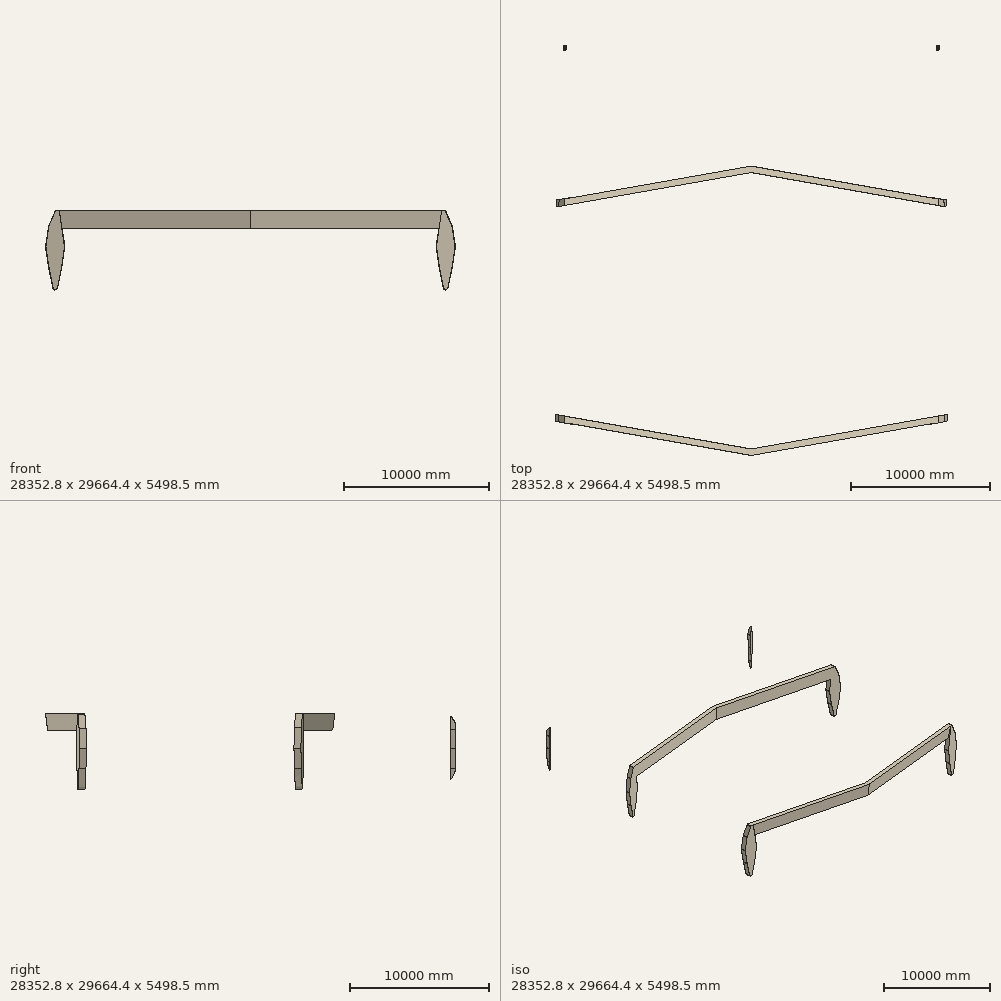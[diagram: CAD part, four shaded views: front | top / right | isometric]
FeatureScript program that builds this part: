
annotation { "Feature Type Name" : "Feature", "Feature Type Description" : "" }
export const myFeature = defineFeature(function(context is Context, id is Id, definition is map)
    precondition{}
    {
        {
            var Q0;
            Q0=qCreatedBy(makeId("Front.planeOp"),FACE);
            var sketch = newSketch(context, id + "F0", { "sketchPlane" : qUnion([Q0])});
            skPoint(sketch, "E0.end.orphan", {"position": v(0, 0) * mm});
            skLineSegment(sketch, "E1", {"start": v(0, 0) * mm, "end": v(0, -5500) * mm});
            skLineSegment(sketch, "E2", {"start": v(500, -4000) * mm, "end": v(750, -2500) * mm});
            skFitSpline(sketch, "E3", {"points": [v(0, -5500) * mm, v(189.72, -5319.94) * mm, v(366.95, -4555.93) * mm, v(500, -4000) * mm], "startDerivative": vector(1833.22, 785.24) * mm, "endDerivative": vector(535.36, 2334.8) * mm});
            skLineSegment(sketch, "E4", {"start": v(0, 0) * mm, "end": v(500, -1000) * mm});
            skLineSegment(sketch, "E5", {"start": v(500, -1000) * mm, "end": v(750, -2500) * mm});
            skSolve(sketch);
        }
        {
            var Q0;
            Q0=qCreatedBy(makeId("Front.planeOp"),FACE);
            cPlane(context, id + "F1", {"entities" : qUnion([Q0]), "cplaneType" : CPlaneType.OFFSET, "offset" : 10000 * mm, "oppositeDirection" : true, "width" : 150 * mm, "height" : 150 * mm});
        }
        {
            var Q0;
            Q0=qCreatedBy(id+"F1.planeOp",FACE);
            var sketch = newSketch(context, id + "F2", { "sketchPlane" : qUnion([Q0])});
            skLineSegment(sketch, "E6", {"start": v(0, 0) * mm, "end": v(0, -5500) * mm});
            skFitSpline(sketch, "E7", {"points": [v(0, -5500) * mm, v(174.15, -5265.2) * mm, v(305.11, -4690.98) * mm, v(500, -4000) * mm], "startDerivative": vector(1750.56, 1279.5) * mm, "endDerivative": vector(993.95, 3484.4) * mm});
            skLineSegment(sketch, "E8", {"start": v(500, -4000) * mm, "end": v(750, -2500) * mm});
            skPoint(sketch, "E9.startDerivative.orphan", {"position": v(5091.83, 0) * mm});
            skLineSegment(sketch, "E10", {"start": v(500, -1000) * mm, "end": v(0, 0) * mm});
            skLineSegment(sketch, "E11", {"start": v(750, -2500) * mm, "end": v(500, -1000) * mm});
            skSolve(sketch);
        }
        {
            var Q0;
            Q0=qCreatedBy(id+"F1.planeOp",FACE);
            cPlane(context, id + "F3", {"entities" : qUnion([Q0]), "cplaneType" : CPlaneType.OFFSET, "offset" : 15000 * mm, "oppositeDirection" : true, "width" : 150 * mm, "height" : 150 * mm});
        }
        {
            var Q0;
            Q0=qCreatedBy(id+"F3.planeOp",FACE);
            var sketch = newSketch(context, id + "F4", { "sketchPlane" : qUnion([Q0])});
            skLineSegment(sketch, "E12", {"start": v(0, 0) * mm, "end": v(0, -5500) * mm});
            skLineSegment(sketch, "E13", {"start": v(0, -5500) * mm, "end": v(0, -5500) * mm});
            skLineSegment(sketch, "E14", {"start": v(0, -5500) * mm, "end": v(12.9, -4000) * mm});
            skLineSegment(sketch, "E15", {"start": v(12.9, -4000) * mm, "end": v(85.66, -2500) * mm});
            skLineSegment(sketch, "E16", {"start": v(0, 0) * mm, "end": v(94.2, -1134.32) * mm});
            skLineSegment(sketch, "E17", {"start": v(94.2, -1134.32) * mm, "end": v(85.66, -2500) * mm});
            skSolve(sketch);
        }
        {
            var Q0;
            Q0=qCreatedBy(makeId("Front.planeOp"),FACE);
            cPlane(context, id + "F5", {"entities" : qUnion([Q0]), "cplaneType" : CPlaneType.OFFSET, "offset" : 10000 * mm, "width" : 150 * mm, "height" : 150 * mm});
        }
        {
            var Q0;
            Q0=qCreatedBy(id+"F5.planeOp",FACE);
            var sketch = newSketch(context, id + "F6", { "sketchPlane" : qUnion([Q0])});
            skLineSegment(sketch, "E18", {"start": v(0, -500) * mm, "end": v(0, -5500) * mm});
            skLineSegment(sketch, "E19", {"start": v(0, -5500) * mm, "end": v(14.37, -4000) * mm});
            skLineSegment(sketch, "E20", {"start": v(14.37, -4000) * mm, "end": v(85.96, -2500) * mm});
            skPoint(sketch, "E21", {"position": v(51.72, -1902.5) * mm});
            skLineSegment(sketch, "E22", {"start": v(94.34, -1565.05) * mm, "end": v(85.96, -2500) * mm});
            skLineSegment(sketch, "E23", {"start": v(0, -500) * mm, "end": v(94.34, -1565.05) * mm});
            skSolve(sketch);
        }
        {
            var Q0;
            Q0=makeQuery(id+"F4.imprint","IMPRINT",FACE,{"disambiguationData":[TD([[makeQuery(id+"F4.imprint","IMPRINT",EDGE,{"derivedFrom":sQuery(id+"F4.wireOp",EDGE,"E12")}),1.0]])]});
            var Q1;
            Q1=makeQuery(id+"F2.imprint","IMPRINT",FACE,{"disambiguationData":[TD([[makeQuery(id+"F2.imprint","IMPRINT",EDGE,{"derivedFrom":sQuery(id+"F2.wireOp",EDGE,"E6")}),1.0]])]});
            var Q2;
            Q2=makeQuery(id+"F0.imprint","IMPRINT",FACE,{"disambiguationData":[TD([[makeQuery(id+"F0.imprint","IMPRINT",EDGE,{"derivedFrom":sQuery(id+"F0.wireOp",EDGE,"E1")}),1.0]])]});
            var Q3;
            Q3=makeQuery(id+"F6.imprint","IMPRINT",FACE,{"disambiguationData":[TD([[makeQuery(id+"F6.imprint","IMPRINT",EDGE,{"derivedFrom":sQuery(id+"F6.wireOp",EDGE,"E18")}),1.0]])]});
            var Q4;
            Q4=sQuery(id+"F4.wireOp",EDGE,"E14");
            var Q5;
            Q5=sQuery(id+"F2.wireOp",EDGE,"E8");
            var Q6;
            Q6=sQuery(id+"F4.wireOp",EDGE,"E15");
            var Q7;
            Q7=sQuery(id+"F4.wireOp",EDGE,"sgJCfSwm-QjFF-VmRN-4AcW-iuittDDyERBM");
            loft(context, id + "F7", {"sheetProfilesArray" : [{ "sheetProfileEntities" : qUnion([Q0]) }, { "sheetProfileEntities" : qUnion([Q1]) }, { "sheetProfileEntities" : qUnion([Q2]) }, { "sheetProfileEntities" : qUnion([Q3]) }], "guidesArray" : [{ "guideEntities" : qUnion([Q4]), "guideDerivativeType" : LoftGuideDerivativeType.DEFAULT, "guideDerivativeMagnitude" : 1 }, { "guideEntities" : qUnion([Q5]), "guideDerivativeType" : LoftGuideDerivativeType.DEFAULT, "guideDerivativeMagnitude" : 1 }, { "guideEntities" : qUnion([Q6]), "guideDerivativeType" : LoftGuideDerivativeType.DEFAULT, "guideDerivativeMagnitude" : 1 }, { "guideEntities" : qUnion([Q7]), "guideDerivativeType" : LoftGuideDerivativeType.DEFAULT, "guideDerivativeMagnitude" : 1 }]});
        }
        {
            var Q0;
            Q0=makeQuery(id+"F7.opLoft","SWEPT_BODY",BODY,{"disambiguationData":[OSD([sQuery(id+"F0.wireOp",EDGE,"E3"),sQuery(id+"F2.wireOp",EDGE,"E7"),makeQuery(id+"F4.imprint","IMPRINT",FACE,{"disambiguationData":[TD([[makeQuery(id+"F4.imprint","IMPRINT",EDGE,{"derivedFrom":sQuery(id+"F4.wireOp",EDGE,"E12")}),1.0]])]}),makeQuery(id+"F6.imprint","IMPRINT",FACE,{"disambiguationData":[TD([[makeQuery(id+"F6.imprint","IMPRINT",EDGE,{"derivedFrom":sQuery(id+"F6.wireOp",EDGE,"E18")}),1.0]])]})])]});
            var Q1;
            Q1=qCreatedBy(makeId("Right.planeOp"),FACE);
            mirror(context, id + "F8", {"operationType" : NewBodyOperationType.ADD, "entities" : qUnion([Q0]), "mirrorPlane" : qUnion([Q1])});
        }
        {
            var Q0;
            {var subQ0=makeQuery(id+"F7.opLoft","SWEPT_EDGE",EDGE,{"disambiguationData":[OSD([sQuery(id+"F0.wireOp",EDGE,"E1"),sQuery(id+"F0.wireOp",EDGE,"E3"),sQuery(id+"F6.wireOp",EDGE,"E18"),sQuery(id+"F6.wireOp",EDGE,"E19")])]});Q0=makeQuery(id+"F8.boolean.opBoolean","MERGE",EDGE,{"derivedFrom":[subQ0,makeQuery(id+"F8.opPattern","COPY",EDGE,{"derivedFrom":subQ0,"instanceName":"1"})]});}
            fillet(context, id + "F9", {"entities" : qUnion([Q0]), "radius" : 12 * mm, "tangentPropagation" : true, "allowEdgeOverflow" : false});
        }
        {
            var Q0;
            Q0=qCreatedBy(makeId("Front.planeOp"),FACE);
            var sketch = newSketch(context, id + "F10", { "sketchPlane" : qUnion([Q0])});
            skLineSegment(sketch, "E24", {"start": v(0, 0) * mm, "end": v(0, -5082.07) * mm, "construction": true});
            skLineSegment(sketch, "E25", {"start": v(-7000, 3102.27) * mm, "end": v(-7000, -5771.46) * mm, "construction": true});
            skLineSegment(sketch, "E26", {"start": v(-7000, 0) * mm, "end": v(-13500, 0) * mm});
            skLineSegment(sketch, "E27", {"start": v(-13500, 0) * mm, "end": v(-13500, -1000) * mm});
            skLineSegment(sketch, "E28", {"start": v(-13500, -1000) * mm, "end": v(-7000, -1000) * mm});
            skLineSegment(sketch, "E29", {"start": v(-7000, -1000) * mm, "end": v(0, -1000) * mm});
            skLineSegment(sketch, "E30", {"start": v(0, 0) * mm, "end": v(0, -1000) * mm});
            skLineSegment(sketch, "E31", {"start": v(-7000, 0) * mm, "end": v(0, 0) * mm});
            skSolve(sketch);
        }
        {
            var Q0;
            Q0=makeQuery(id+"F10.imprint","IMPRINT",FACE,{"disambiguationData":[TD([[makeQuery(id+"F10.imprint","IMPRINT",EDGE,{"derivedFrom":sQuery(id+"F10.wireOp",EDGE,"3sFQAXWc-wyO7-hPk9-7dSX-oAIZwABY1ojd")}),1.0]])]});
            var Q1;
            Q1=makeQuery(id+"F10.imprint","IMPRINT",FACE,{"disambiguationData":[TD([[makeQuery(id+"F10.imprint","IMPRINT",EDGE,{"derivedFrom":sQuery(id+"F10.wireOp",EDGE,"E26")}),1.0]])]});
            extrude(context, id + "F11", {"entities" : qUnion([Q0, Q1]), "endBound" : BoundingType.SYMMETRIC, "oppositeDirection" : true, "depth" : 37400 * mm});
        }
        {
            var Q0;
            Q0=qCreatedBy(makeId("Top.planeOp"),FACE);
            var sketch = newSketch(context, id + "F12", { "sketchPlane" : qUnion([Q0])});
            skLineSegment(sketch, "E32.bottom", {"start": v(-13500, 24621.28) * mm, "end": v(7276.55, 24621.28) * mm});
            skLineSegment(sketch, "E32.left", {"start": v(-13500, 24621.28) * mm, "end": v(-13500, 16304.47) * mm});
            skLineSegment(sketch, "E32.right", {"start": v(7276.55, 24621.28) * mm, "end": v(7276.55, 18829) * mm});
            skLineSegment(sketch, "E33.left", {"start": v(-13500, 15804.47) * mm, "end": v(-13500, -4195.53) * mm});
            skLineSegment(sketch, "E33.right", {"start": v(8153.2, 18329) * mm, "end": v(8153.2, -1671) * mm});
            skLineSegment(sketch, "E34.top", {"start": v(-13500, -21040.08) * mm, "end": v(8250.14, -21040.08) * mm});
            skLineSegment(sketch, "E34.left", {"start": v(-13500, -4695.53) * mm, "end": v(-13500, -21040.08) * mm});
            skLineSegment(sketch, "E34.right", {"start": v(8250.14, -2171) * mm, "end": v(8250.14, -21040.08) * mm});
            skLineSegment(sketch, "E35", {"start": v(0, -1047.14) * mm, "end": v(-1927.45, -1047.14) * mm, "construction": true});
            skLineSegment(sketch, "E36", {"start": v(0, 2086.97) * mm, "end": v(-2089.7, 2086.97) * mm, "construction": true});
            skLineSegment(sketch, "E37", {"start": v(-13500, 23613.23) * mm, "end": v(-13500, -27703.45) * mm, "construction": true});
            skLineSegment(sketch, "E38", {"start": v(-13500, 16304.47) * mm, "end": v(8153.2, 12486.43) * mm});
            skLineSegment(sketch, "E39", {"start": v(-13500, 15804.47) * mm, "end": v(8153.2, 11986.43) * mm});
            skLineSegment(sketch, "E40", {"start": v(-13500, -4195.53) * mm, "end": v(8153.2, -377.49) * mm});
            skLineSegment(sketch, "E41", {"start": v(-13500, -4695.53) * mm, "end": v(8153.2, -877.49) * mm});
            skLineSegment(sketch, "E42", {"start": v(7276.55, 18829) * mm, "end": v(8153.2, 18329) * mm});
            skLineSegment(sketch, "E43", {"start": v(8153.2, -1671) * mm, "end": v(8250.14, -2171) * mm});
            skSolve(sketch);
        }
        {
            var Q0;
            Q0=makeQuery(id+"F12.imprint","IMPRINT",FACE,{"disambiguationData":[TD([[makeQuery(id+"F12.imprint","IMPRINT",EDGE,{"derivedFrom":sQuery(id+"F12.wireOp",EDGE,"E32.bottom")}),-1.0]])]});
            var Q1;
            Q1=makeQuery(id+"F12.imprint","IMPRINT",FACE,{"disambiguationData":[TD([[makeQuery(id+"F12.imprint","IMPRINT",EDGE,{"derivedFrom":sQuery(id+"F12.wireOp",EDGE,"E33.left")}),1.0]])]});
            var Q2;
            Q2=makeQuery(id+"F12.imprint","IMPRINT",FACE,{"disambiguationData":[TD([[makeQuery(id+"F12.imprint","IMPRINT",EDGE,{"derivedFrom":sQuery(id+"F12.wireOp",EDGE,"E34.top")}),1.0]])]});
            extrude(context, id + "F13", {"entities" : qUnion([Q0, Q1, Q2]), "operationType" : NewBodyOperationType.REMOVE, "endBound" : BoundingType.SYMMETRIC, "oppositeDirection" : true, "depth" : 13225 * mm});
        }
        {
            var Q0;
            Q0=makeQuery(id+"F7.opLoft","SWEPT_BODY",BODY,{"disambiguationData":[OSD([sQuery(id+"F0.wireOp",EDGE,"E4"),sQuery(id+"F2.wireOp",EDGE,"E8"),makeQuery(id+"F4.imprint","IMPRINT",FACE,{"disambiguationData":[TD([[makeQuery(id+"F4.imprint","IMPRINT",EDGE,{"derivedFrom":sQuery(id+"F4.wireOp",EDGE,"E12")}),1.0]])]}),makeQuery(id+"F6.imprint","IMPRINT",FACE,{"disambiguationData":[TD([[makeQuery(id+"F6.imprint","IMPRINT",EDGE,{"derivedFrom":sQuery(id+"F6.wireOp",EDGE,"E18")}),1.0]])]})])]});
            var Q1;
            Q1=makeQuery(id+"F11.opExtrude","SWEPT_BODY",BODY,{"disambiguationData":[OSD([sQuery(id+"F10.wireOp",EDGE,"E26"),sQuery(id+"F10.wireOp",EDGE,"E27"),sQuery(id+"F10.wireOp",EDGE,"E28"),sQuery(id+"F10.wireOp",EDGE,"E29"),sQuery(id+"F10.wireOp",EDGE,"E30"),sQuery(id+"F10.wireOp",EDGE,"E31")])]});
            var Q2;
            Q2=makeQuery(id+"F11.opExtrude","SWEPT_FACE",FACE,{"disambiguationData":[OSD([sQuery(id+"F10.wireOp",EDGE,"E27")])]});
            mirror(context, id + "F14", {"operationType" : NewBodyOperationType.ADD, "entities" : qUnion([Q0, Q1]), "mirrorPlane" : qUnion([Q2])});
        }
        {
            var Q0;
            Q0=qCreatedBy(makeId("Right.planeOp"),FACE);
            var sketch = newSketch(context, id + "F15", { "sketchPlane" : qUnion([Q0])});
            skLineSegment(sketch, "E44", {"start": v(25015.3, -3553.39) * mm, "end": v(25015.3, -1000) * mm});
            skLineSegment(sketch, "E45", {"start": v(24015.3, 0) * mm, "end": v(13594.14, 0) * mm});
            skLineSegment(sketch, "E46", {"start": v(13594.14, 0) * mm, "end": v(12052.37, 3741.26) * mm});
            skLineSegment(sketch, "E47", {"start": v(12052.37, 3741.26) * mm, "end": v(25847.84, 3035.2) * mm});
            skLineSegment(sketch, "E48", {"start": v(25847.84, 3035.2) * mm, "end": v(26929.87, 1249.84) * mm});
            skLineSegment(sketch, "E49", {"start": v(26929.87, 1249.84) * mm, "end": v(25015.3, -3553.39) * mm});
            skPoint(sketch, "E50.visualSharp", {"position": v(25015.3, 0) * mm});
            skArc(sketch, "E50.filletArc", {"start": v(25015.3, -1000) * mm, "mid": v(24722.4, -292.9) * mm, "end": v(24015.3, 0) * mm});
            skLineSegment(sketch, "E51", {"start": v(-10015.9, -1415.8) * mm, "end": v(-10015.9, -3965.22) * mm});
            skLineSegment(sketch, "E52", {"start": v(-10015.9, -3965.22) * mm, "end": v(-12936.5, -3419.61) * mm});
            skLineSegment(sketch, "E53", {"start": v(-12936.5, -3419.61) * mm, "end": v(-12936.5, 1047.72) * mm});
            skLineSegment(sketch, "E54", {"start": v(-12936.5, 1047.72) * mm, "end": v(-5974.96, 1396.63) * mm});
            skPoint(sketch, "E55.visualSharp", {"position": v(-10015.9, 0) * mm});
            skPoint(sketch, "E56.visualSharp", {"position": v(-10015.9, -509.7) * mm});
            skArc(sketch, "E56.filletArc", {"start": v(-9114.2, -420.64) * mm, "mid": v(-9756.95, -744.34) * mm, "end": v(-10015.9, -1415.8) * mm});
            skLineSegment(sketch, "E57", {"start": v(-5974.96, 1396.63) * mm, "end": v(-4930.65, -171.54) * mm});
            skLineSegment(sketch, "E58", {"start": v(-4930.65, -171.54) * mm, "end": v(-9114.2, -420.64) * mm});
            skSolve(sketch);
        }
        {
            var Q0;
            Q0=makeQuery(id+"F15.imprint","IMPRINT",FACE,{"disambiguationData":[TD([[makeQuery(id+"F15.imprint","IMPRINT",EDGE,{"derivedFrom":sQuery(id+"F15.wireOp",EDGE,"E51")}),-1.0]])]});
            var Q1;
            Q1=makeQuery(id+"F15.imprint","IMPRINT",FACE,{"disambiguationData":[TD([[makeQuery(id+"F15.imprint","IMPRINT",EDGE,{"derivedFrom":sQuery(id+"F15.wireOp",EDGE,"E44")}),-1.0]])]});
            extrude(context, id + "F16", {"entities" : qUnion([Q0, Q1]), "operationType" : NewBodyOperationType.REMOVE, "endBound" : BoundingType.SYMMETRIC, "oppositeDirection" : true, "depth" : 88000 * mm});
        }
        {
            var Q0;
            {var subQ0=makeQuery(id+"F13.boolean.opBoolean","SPLIT",FACE,{"disambiguationData":[TD([makeQuery(id+"F13.opExtrude","SWEPT_FACE",FACE,{"disambiguationData":[OSD([sQuery(id+"F12.wireOp",EDGE,"E40")])]})])],"derivedFrom":makeQuery(id+"F11.opExtrude","SWEPT_FACE",FACE,{"disambiguationData":[OSD([sQuery(id+"F10.wireOp",EDGE,"E28"),sQuery(id+"F10.wireOp",EDGE,"E29")])]})});Q0=makeQuery(id+"F14.boolean.opBoolean","MERGE",FACE,{"derivedFrom":[subQ0,makeQuery(id+"F14.opPattern","COPY",FACE,{"derivedFrom":subQ0,"instanceName":"1"})]});}
            var Q1;
            {var subQ0=makeQuery(id+"F13.boolean.opBoolean","SPLIT",FACE,{"disambiguationData":[TD([makeQuery(id+"F13.opExtrude","SWEPT_FACE",FACE,{"disambiguationData":[OSD([sQuery(id+"F12.wireOp",EDGE,"E38")])]})])],"derivedFrom":makeQuery(id+"F11.opExtrude","SWEPT_FACE",FACE,{"disambiguationData":[OSD([sQuery(id+"F10.wireOp",EDGE,"E28"),sQuery(id+"F10.wireOp",EDGE,"E29")])]})});Q1=makeQuery(id+"F14.boolean.opBoolean","MERGE",FACE,{"derivedFrom":[subQ0,makeQuery(id+"F14.opPattern","COPY",FACE,{"derivedFrom":subQ0,"instanceName":"1"})]});}
            extrude(context, id + "F17", {"entities" : qUnion([Q0, Q1]), "operationType" : NewBodyOperationType.ADD, "depth" : 250 * mm});
        }
        {
            var Q0;
            {var subQ0=sQuery(id+"F12.wireOp",EDGE,"E41");var subQ1=sQuery(id+"F10.wireOp",EDGE,"E29");var subQ2=sQuery(id+"F10.wireOp",EDGE,"E28");Q0=makeQuery(id+"F17.opExtrude","CAP_EDGE",EDGE,{"disambiguationData":[OSD([subQ2,subQ1,subQ0]),TDD([makeQuery(id+"F13.boolean.opBoolean","INTERSECT",EDGE,{"derivedFrom":[makeQuery(id+"F11.opExtrude","SWEPT_FACE",FACE,{"disambiguationData":[OSD([subQ2,subQ1])]}),makeQuery(id+"F13.opExtrude","SWEPT_FACE",FACE,{"disambiguationData":[OSD([subQ0])]})]})])],"isStart":false});}
            var Q1;
            {var subQ0=sQuery(id+"F12.wireOp",EDGE,"E41");var subQ1=sQuery(id+"F10.wireOp",EDGE,"E29");var subQ2=sQuery(id+"F10.wireOp",EDGE,"E28");Q1=makeQuery(id+"F17.opExtrude","CAP_EDGE",EDGE,{"disambiguationData":[OSD([subQ2,subQ1,subQ0]),TDD([makeQuery(id+"F14.opPattern","COPY",EDGE,{"derivedFrom":makeQuery(id+"F13.boolean.opBoolean","INTERSECT",EDGE,{"derivedFrom":[makeQuery(id+"F11.opExtrude","SWEPT_FACE",FACE,{"disambiguationData":[OSD([subQ2,subQ1])]}),makeQuery(id+"F13.opExtrude","SWEPT_FACE",FACE,{"disambiguationData":[OSD([subQ0])]})]}),"instanceName":"1"})])],"isStart":false});}
            var Q2;
            {var subQ0=sQuery(id+"F12.wireOp",EDGE,"E38");var subQ1=sQuery(id+"F10.wireOp",EDGE,"E29");var subQ2=sQuery(id+"F10.wireOp",EDGE,"E28");Q2=makeQuery(id+"F17.opExtrude","CAP_EDGE",EDGE,{"disambiguationData":[OSD([subQ2,subQ1,subQ0]),TDD([makeQuery(id+"F14.opPattern","COPY",EDGE,{"derivedFrom":makeQuery(id+"F13.boolean.opBoolean","INTERSECT",EDGE,{"derivedFrom":[makeQuery(id+"F11.opExtrude","SWEPT_FACE",FACE,{"disambiguationData":[OSD([subQ2,subQ1])]}),makeQuery(id+"F13.opExtrude","SWEPT_FACE",FACE,{"disambiguationData":[OSD([subQ0])]})]}),"instanceName":"1"})])],"isStart":false});}
            chamfer(context, id + "F18", {"entities" : qUnion([Q0, Q1, Q2]), "chamferType" : ChamferType.OFFSET_ANGLE, "width" : 1500 * mm, "oppositeDirection" : true, "angle" : 7 * degree, "tangentPropagation" : true});
        }
        {
            var Q0;
            {var subQ0=sQuery(id+"F12.wireOp",EDGE,"E38");var subQ1=sQuery(id+"F10.wireOp",EDGE,"E29");var subQ2=sQuery(id+"F10.wireOp",EDGE,"E28");Q0=makeQuery(id+"F17.opExtrude","CAP_EDGE",EDGE,{"disambiguationData":[OSD([subQ2,subQ1,subQ0]),TDD([makeQuery(id+"F13.boolean.opBoolean","INTERSECT",EDGE,{"derivedFrom":[makeQuery(id+"F11.opExtrude","SWEPT_FACE",FACE,{"disambiguationData":[OSD([subQ2,subQ1])]}),makeQuery(id+"F13.opExtrude","SWEPT_FACE",FACE,{"disambiguationData":[OSD([subQ0])]})]})])],"isStart":false});}
            chamfer(context, id + "F19", {"entities" : qUnion([Q0]), "chamferType" : ChamferType.OFFSET_ANGLE, "width" : 1500 * mm, "oppositeDirection" : false, "angle" : 7 * degree, "tangentPropagation" : true});
        }
    });
